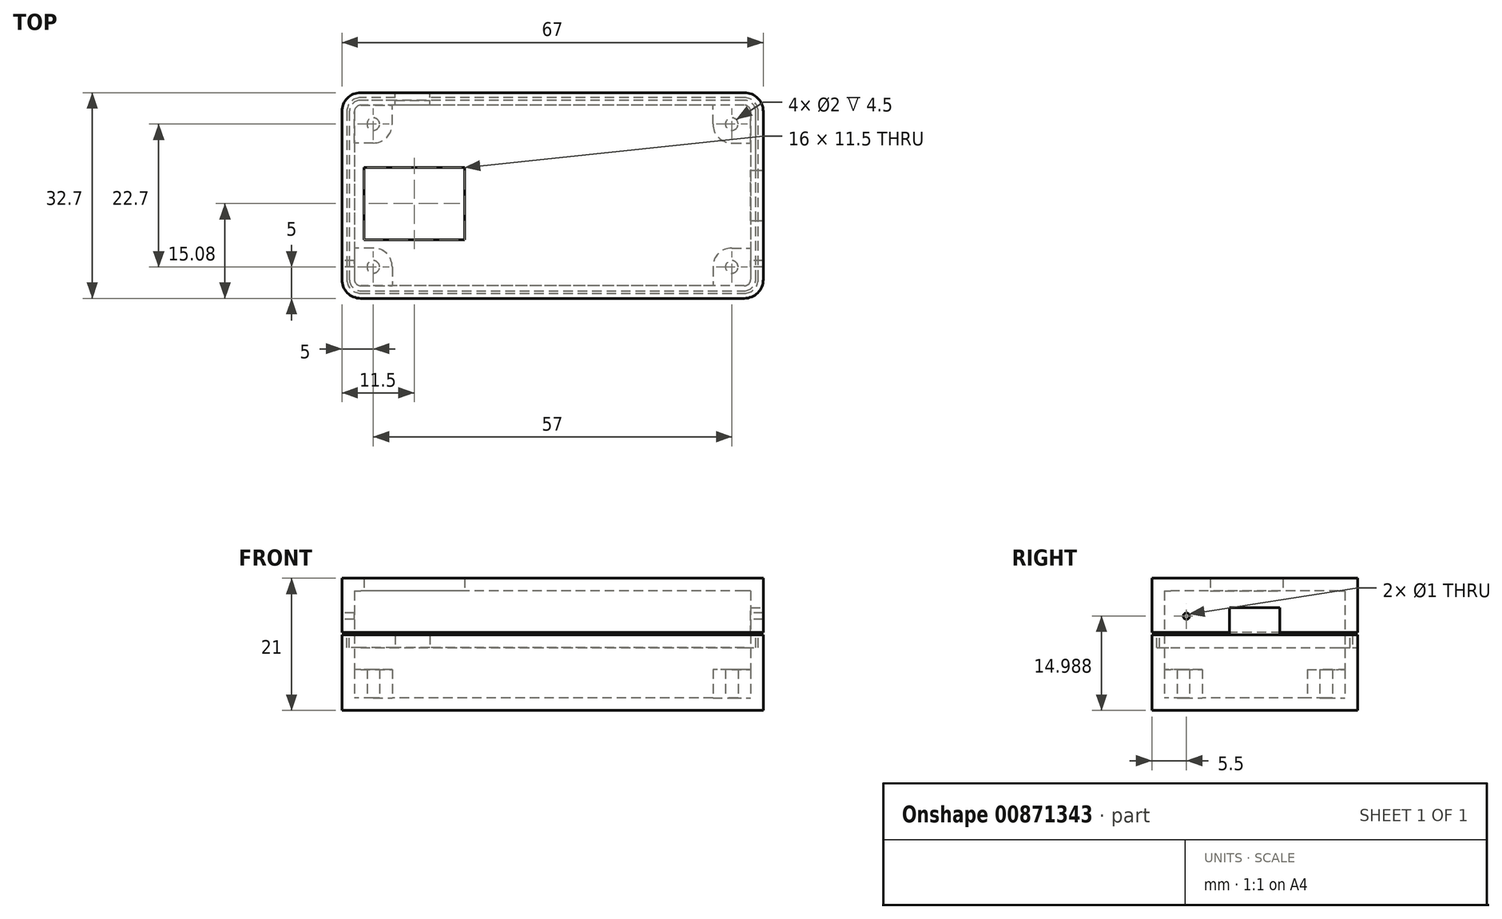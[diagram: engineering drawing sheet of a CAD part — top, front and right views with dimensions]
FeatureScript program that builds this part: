
annotation { "Feature Type Name" : "Feature", "Feature Type Description" : "" }
export const myFeature = defineFeature(function(context is Context, id is Id, definition is map)
    precondition{}
    {
        {
            var Q0;
            Q0=qCreatedBy(makeId("Top.planeOp"),FACE);
            var sketch = newSketch(context, id + "F0", { "sketchPlane" : qUnion([Q0])});
            skLineSegment(sketch, "E0.bottom", {"start": v(33.5, 16.35) * mm, "end": v(-33.5, 16.35) * mm});
            skLineSegment(sketch, "E0.top", {"start": v(33.5, -16.35) * mm, "end": v(-33.5, -16.35) * mm});
            skLineSegment(sketch, "E0.left", {"start": v(33.5, 16.35) * mm, "end": v(33.5, -16.35) * mm});
            skLineSegment(sketch, "E0.right", {"start": v(-33.5, 16.35) * mm, "end": v(-33.5, -16.35) * mm});
            skPoint(sketch, "E0.middle", {"position": v(0, 0) * mm});
            skSolve(sketch);
        }
        {
            var Q0;
            Q0=makeQuery(id+"F0.imprint","IMPRINT",FACE,{"disambiguationData":[TD([[makeQuery(id+"F0.imprint","IMPRINT",EDGE,{"derivedFrom":sQuery(id+"F0.wireOp",EDGE,"E0.bottom")}),1.0]])]});
            extrude(context, id + "F1", {"entities" : qUnion([Q0]), "depth" : 11 * mm, "offsetDistance" : 25 * mm});
        }
        {
            var Q0;
            Q0=makeQuery(id+"F1.opExtrude","SWEPT_EDGE",EDGE,{"disambiguationData":[OSD([sQuery(id+"F0.wireOp",EDGE,"E0.top"),sQuery(id+"F0.wireOp",EDGE,"E0.left")])]});
            var Q1;
            Q1=makeQuery(id+"F1.opExtrude","SWEPT_EDGE",EDGE,{"disambiguationData":[OSD([sQuery(id+"F0.wireOp",EDGE,"E0.bottom"),sQuery(id+"F0.wireOp",EDGE,"E0.left")])]});
            var Q2;
            Q2=makeQuery(id+"F1.opExtrude","SWEPT_EDGE",EDGE,{"disambiguationData":[OSD([sQuery(id+"F0.wireOp",EDGE,"E0.top"),sQuery(id+"F0.wireOp",EDGE,"E0.right")])]});
            var Q3;
            Q3=makeQuery(id+"F1.opExtrude","SWEPT_EDGE",EDGE,{"disambiguationData":[OSD([sQuery(id+"F0.wireOp",EDGE,"E0.bottom"),sQuery(id+"F0.wireOp",EDGE,"E0.right")])]});
            fillet(context, id + "F2", {"entities" : qUnion([Q0, Q1, Q2, Q3]), "radius" : 3 * mm, "tangentPropagation" : true, "allowEdgeOverflow" : false});
        }
        {
            var Q0;
            Q0=makeQuery(id+"F1.opExtrude","CAP_FACE",FACE,{"disambiguationData":[OSD([sQuery(id+"F0.wireOp",EDGE,"E0.bottom"),sQuery(id+"F0.wireOp",EDGE,"E0.top"),sQuery(id+"F0.wireOp",EDGE,"E0.left"),sQuery(id+"F0.wireOp",EDGE,"E0.right")])],"isStart":true});
            extrude(context, id + "F3", {"entities" : qUnion([Q0]), "depth" : 10 * mm, "offsetDistance" : 25 * mm});
        }
        {
            var Q0;
            Q0=makeQuery(id+"F1.opExtrude","CAP_FACE",FACE,{"disambiguationData":[OSD([sQuery(id+"F0.wireOp",EDGE,"E0.bottom"),sQuery(id+"F0.wireOp",EDGE,"E0.top"),sQuery(id+"F0.wireOp",EDGE,"E0.left"),sQuery(id+"F0.wireOp",EDGE,"E0.right")])],"isStart":true});
            shell(context, id + "F4", {"entities" : qUnion([Q0]), "thickness" : 2 * mm});
        }
        {
            var Q0;
            Q0=makeQuery(id+"F3.opExtrude","CAP_FACE",FACE,{"disambiguationData":[OSD([sQuery(id+"F0.wireOp",EDGE,"E0.bottom"),sQuery(id+"F0.wireOp",EDGE,"E0.top"),sQuery(id+"F0.wireOp",EDGE,"E0.left"),sQuery(id+"F0.wireOp",EDGE,"E0.right")])],"isStart":true});
            shell(context, id + "F5", {"entities" : qUnion([Q0]), "thickness" : 2 * mm});
        }
        {
            var Q0;
            Q0=makeQuery(id+"F0.imprint","IMPRINT",FACE,{"disambiguationData":[TD([[makeQuery(id+"F0.imprint","IMPRINT",EDGE,{"derivedFrom":sQuery(id+"F0.wireOp",EDGE,"E0.bottom")}),1.0]])]});
            extrude(context, id + "F6", {"entities" : qUnion([Q0]), "operationType" : NewBodyOperationType.REMOVE, "depth" : 2.4 * mm, "offsetDistance" : 25 * mm});
        }
        {
            var Q0;
            Q0=qCreatedBy(makeId("Right.planeOp"),FACE);
            var sketch = newSketch(context, id + "F7", { "sketchPlane" : qUnion([Q0])});
            skLineSegment(sketch, "E1.bottom", {"start": v(-16.35, 0) * mm, "end": v(-15.55, 0) * mm});
            skLineSegment(sketch, "E1.top", {"start": v(-16.35, 2) * mm, "end": v(-15.55, 2) * mm});
            skLineSegment(sketch, "E1.left", {"start": v(-16.35, 0) * mm, "end": v(-16.35, 2) * mm});
            skLineSegment(sketch, "E1.right", {"start": v(-15.55, 0) * mm, "end": v(-15.55, 2) * mm});
            skLineSegment(sketch, "E2.bottom", {"start": v(-14.35, 0) * mm, "end": v(-15.15, 0) * mm});
            skLineSegment(sketch, "E2.top", {"start": v(-14.35, 2.4) * mm, "end": v(-15.15, 2.4) * mm});
            skLineSegment(sketch, "E2.left", {"start": v(-14.35, 0) * mm, "end": v(-14.35, 2.4) * mm});
            skLineSegment(sketch, "E2.right", {"start": v(-15.15, 0) * mm, "end": v(-15.15, 2.4) * mm});
            skSolve(sketch);
        }
        {
            var Q0;
            Q0=makeQuery(id+"F7.imprint","IMPRINT",FACE,{"disambiguationData":[TD([[makeQuery(id+"F7.imprint","IMPRINT",EDGE,{"derivedFrom":sQuery(id+"F7.wireOp",EDGE,"E1.bottom")}),1.0]])]});
            var Q1;
            Q1=makeQuery(id+"F3.opExtrude","CAP_EDGE",EDGE,{"disambiguationData":[OSD([sQuery(id+"F0.wireOp",EDGE,"E0.top")])],"isStart":true});
            var Q2;
            {var subQ0=sQuery(id+"F0.wireOp",EDGE,"E0.right");var subQ1=sQuery(id+"F0.wireOp",EDGE,"E0.left");var subQ2=sQuery(id+"F0.wireOp",EDGE,"E0.top");var subQ3=sQuery(id+"F0.wireOp",EDGE,"E0.bottom");Q2=makeQuery(id+"F3.opExtrude","CAP_EDGE",EDGE,{"disambiguationData":[OSD([subQ3,subQ2,subQ1,subQ0]),TDD([makeQuery(id+"F2.opFillet","BLEND_EDGE",EDGE,{"blendedFrom":[makeQuery(id+"F1.opExtrude","SWEPT_EDGE",EDGE,{"disambiguationData":[OSD([subQ2,subQ1])]}),makeQuery(id+"F1.opExtrude","CAP_FACE",FACE,{"disambiguationData":[OSD([subQ3,subQ2,subQ1,subQ0])],"isStart":true})],"blendedInto":[makeQuery(id+"F1.opExtrude","CAP_FACE",FACE,{"disambiguationData":[OSD([subQ3,subQ2,subQ1,subQ0])],"isStart":true})]})])],"isStart":true});}
            var Q3;
            Q3=makeQuery(id+"F3.opExtrude","CAP_EDGE",EDGE,{"disambiguationData":[OSD([sQuery(id+"F0.wireOp",EDGE,"E0.left")])],"isStart":true});
            var Q4;
            {var subQ0=sQuery(id+"F0.wireOp",EDGE,"E0.right");var subQ1=sQuery(id+"F0.wireOp",EDGE,"E0.left");var subQ2=sQuery(id+"F0.wireOp",EDGE,"E0.top");var subQ3=sQuery(id+"F0.wireOp",EDGE,"E0.bottom");Q4=makeQuery(id+"F3.opExtrude","CAP_EDGE",EDGE,{"disambiguationData":[OSD([subQ3,subQ2,subQ1,subQ0]),TDD([makeQuery(id+"F2.opFillet","BLEND_EDGE",EDGE,{"blendedFrom":[makeQuery(id+"F1.opExtrude","SWEPT_EDGE",EDGE,{"disambiguationData":[OSD([subQ3,subQ1])]}),makeQuery(id+"F1.opExtrude","CAP_FACE",FACE,{"disambiguationData":[OSD([subQ3,subQ2,subQ1,subQ0])],"isStart":true})],"blendedInto":[makeQuery(id+"F1.opExtrude","CAP_FACE",FACE,{"disambiguationData":[OSD([subQ3,subQ2,subQ1,subQ0])],"isStart":true})]})])],"isStart":true});}
            var Q5;
            Q5=makeQuery(id+"F3.opExtrude","CAP_EDGE",EDGE,{"disambiguationData":[OSD([sQuery(id+"F0.wireOp",EDGE,"E0.bottom")])],"isStart":true});
            var Q6;
            {var subQ0=sQuery(id+"F0.wireOp",EDGE,"E0.right");var subQ1=sQuery(id+"F0.wireOp",EDGE,"E0.left");var subQ2=sQuery(id+"F0.wireOp",EDGE,"E0.top");var subQ3=sQuery(id+"F0.wireOp",EDGE,"E0.bottom");Q6=makeQuery(id+"F3.opExtrude","CAP_EDGE",EDGE,{"disambiguationData":[OSD([subQ3,subQ2,subQ1,subQ0]),TDD([makeQuery(id+"F2.opFillet","BLEND_EDGE",EDGE,{"blendedFrom":[makeQuery(id+"F1.opExtrude","SWEPT_EDGE",EDGE,{"disambiguationData":[OSD([subQ3,subQ0])]}),makeQuery(id+"F1.opExtrude","CAP_FACE",FACE,{"disambiguationData":[OSD([subQ3,subQ2,subQ1,subQ0])],"isStart":true})],"blendedInto":[makeQuery(id+"F1.opExtrude","CAP_FACE",FACE,{"disambiguationData":[OSD([subQ3,subQ2,subQ1,subQ0])],"isStart":true})]})])],"isStart":true});}
            var Q7;
            Q7=makeQuery(id+"F3.opExtrude","CAP_EDGE",EDGE,{"disambiguationData":[OSD([sQuery(id+"F0.wireOp",EDGE,"E0.right")])],"isStart":true});
            var Q8;
            {var subQ0=sQuery(id+"F0.wireOp",EDGE,"E0.right");var subQ1=sQuery(id+"F0.wireOp",EDGE,"E0.left");var subQ2=sQuery(id+"F0.wireOp",EDGE,"E0.top");var subQ3=sQuery(id+"F0.wireOp",EDGE,"E0.bottom");Q8=makeQuery(id+"F3.opExtrude","CAP_EDGE",EDGE,{"disambiguationData":[OSD([subQ3,subQ2,subQ1,subQ0]),TDD([makeQuery(id+"F2.opFillet","BLEND_EDGE",EDGE,{"blendedFrom":[makeQuery(id+"F1.opExtrude","SWEPT_EDGE",EDGE,{"disambiguationData":[OSD([subQ2,subQ0])]}),makeQuery(id+"F1.opExtrude","CAP_FACE",FACE,{"disambiguationData":[OSD([subQ3,subQ2,subQ1,subQ0])],"isStart":true})],"blendedInto":[makeQuery(id+"F1.opExtrude","CAP_FACE",FACE,{"disambiguationData":[OSD([subQ3,subQ2,subQ1,subQ0])],"isStart":true})]})])],"isStart":true});}
            sweep(context, id + "F8", {"operationType" : NewBodyOperationType.ADD, "profiles" : qUnion([Q0]), "path" : qUnion([Q1, Q2, Q3, Q4, Q5, Q6, Q7, Q8])});
        }
        {
            var Q0;
            Q0=makeQuery(id+"F7.imprint","IMPRINT",FACE,{"disambiguationData":[TD([[makeQuery(id+"F7.imprint","IMPRINT",EDGE,{"derivedFrom":sQuery(id+"F7.wireOp",EDGE,"E2.bottom")}),-1.0]])]});
            var Q1;
            Q1=makeQuery(id+"F8.opSweep","SWEPT_EDGE",EDGE,{"disambiguationData":[OSD([sQuery(id+"F0.wireOp",EDGE,"E0.top"),sQuery(id+"F7.wireOp",EDGE,"E1.top"),sQuery(id+"F7.wireOp",EDGE,"E1.left")])]});
            var Q2;
            {var subQ0=sQuery(id+"F7.wireOp",EDGE,"E1.left");var subQ1=sQuery(id+"F7.wireOp",EDGE,"E1.top");var subQ2=sQuery(id+"F0.wireOp",EDGE,"E0.right");var subQ3=sQuery(id+"F0.wireOp",EDGE,"E0.left");var subQ4=sQuery(id+"F0.wireOp",EDGE,"E0.top");var subQ5=sQuery(id+"F0.wireOp",EDGE,"E0.bottom");Q2=makeQuery(id+"F8.opSweep","SWEPT_EDGE",EDGE,{"disambiguationData":[OSD([subQ5,subQ4,subQ3,subQ2,subQ1,subQ0]),TDD([makeQuery(id+"F3.opExtrude","CAP_EDGE",EDGE,{"disambiguationData":[OSD([subQ5,subQ4,subQ3,subQ2]),TDD([makeQuery(id+"F2.opFillet","BLEND_EDGE",EDGE,{"blendedFrom":[makeQuery(id+"F1.opExtrude","SWEPT_EDGE",EDGE,{"disambiguationData":[OSD([subQ4,subQ3])]}),makeQuery(id+"F1.opExtrude","CAP_FACE",FACE,{"disambiguationData":[OSD([subQ5,subQ4,subQ3,subQ2])],"isStart":true})],"blendedInto":[makeQuery(id+"F1.opExtrude","CAP_FACE",FACE,{"disambiguationData":[OSD([subQ5,subQ4,subQ3,subQ2])],"isStart":true})]})])],"isStart":true}),makeQuery(id+"F7.imprint","INTERSECT",VERTEX,{"derivedFrom":[subQ1,subQ0]})])]});}
            var Q3;
            Q3=makeQuery(id+"F8.opSweep","SWEPT_EDGE",EDGE,{"disambiguationData":[OSD([sQuery(id+"F0.wireOp",EDGE,"E0.left"),sQuery(id+"F7.wireOp",EDGE,"E1.top"),sQuery(id+"F7.wireOp",EDGE,"E1.left")])]});
            var Q4;
            {var subQ0=sQuery(id+"F7.wireOp",EDGE,"E1.left");var subQ1=sQuery(id+"F7.wireOp",EDGE,"E1.top");var subQ2=sQuery(id+"F0.wireOp",EDGE,"E0.right");var subQ3=sQuery(id+"F0.wireOp",EDGE,"E0.left");var subQ4=sQuery(id+"F0.wireOp",EDGE,"E0.top");var subQ5=sQuery(id+"F0.wireOp",EDGE,"E0.bottom");Q4=makeQuery(id+"F8.opSweep","SWEPT_EDGE",EDGE,{"disambiguationData":[OSD([subQ5,subQ4,subQ3,subQ2,subQ1,subQ0]),TDD([makeQuery(id+"F3.opExtrude","CAP_EDGE",EDGE,{"disambiguationData":[OSD([subQ5,subQ4,subQ3,subQ2]),TDD([makeQuery(id+"F2.opFillet","BLEND_EDGE",EDGE,{"blendedFrom":[makeQuery(id+"F1.opExtrude","SWEPT_EDGE",EDGE,{"disambiguationData":[OSD([subQ5,subQ3])]}),makeQuery(id+"F1.opExtrude","CAP_FACE",FACE,{"disambiguationData":[OSD([subQ5,subQ4,subQ3,subQ2])],"isStart":true})],"blendedInto":[makeQuery(id+"F1.opExtrude","CAP_FACE",FACE,{"disambiguationData":[OSD([subQ5,subQ4,subQ3,subQ2])],"isStart":true})]})])],"isStart":true}),makeQuery(id+"F7.imprint","INTERSECT",VERTEX,{"derivedFrom":[subQ1,subQ0]})])]});}
            var Q5;
            Q5=makeQuery(id+"F8.opSweep","SWEPT_EDGE",EDGE,{"disambiguationData":[OSD([sQuery(id+"F0.wireOp",EDGE,"E0.bottom"),sQuery(id+"F7.wireOp",EDGE,"E1.top"),sQuery(id+"F7.wireOp",EDGE,"E1.left")])]});
            var Q6;
            {var subQ0=sQuery(id+"F7.wireOp",EDGE,"E1.left");var subQ1=sQuery(id+"F7.wireOp",EDGE,"E1.top");var subQ2=sQuery(id+"F0.wireOp",EDGE,"E0.right");var subQ3=sQuery(id+"F0.wireOp",EDGE,"E0.left");var subQ4=sQuery(id+"F0.wireOp",EDGE,"E0.top");var subQ5=sQuery(id+"F0.wireOp",EDGE,"E0.bottom");Q6=makeQuery(id+"F8.opSweep","SWEPT_EDGE",EDGE,{"disambiguationData":[OSD([subQ5,subQ4,subQ3,subQ2,subQ1,subQ0]),TDD([makeQuery(id+"F3.opExtrude","CAP_EDGE",EDGE,{"disambiguationData":[OSD([subQ5,subQ4,subQ3,subQ2]),TDD([makeQuery(id+"F2.opFillet","BLEND_EDGE",EDGE,{"blendedFrom":[makeQuery(id+"F1.opExtrude","SWEPT_EDGE",EDGE,{"disambiguationData":[OSD([subQ5,subQ2])]}),makeQuery(id+"F1.opExtrude","CAP_FACE",FACE,{"disambiguationData":[OSD([subQ5,subQ4,subQ3,subQ2])],"isStart":true})],"blendedInto":[makeQuery(id+"F1.opExtrude","CAP_FACE",FACE,{"disambiguationData":[OSD([subQ5,subQ4,subQ3,subQ2])],"isStart":true})]})])],"isStart":true}),makeQuery(id+"F7.imprint","INTERSECT",VERTEX,{"derivedFrom":[subQ1,subQ0]})])]});}
            var Q7;
            Q7=makeQuery(id+"F8.opSweep","SWEPT_EDGE",EDGE,{"disambiguationData":[OSD([sQuery(id+"F0.wireOp",EDGE,"E0.right"),sQuery(id+"F7.wireOp",EDGE,"E1.top"),sQuery(id+"F7.wireOp",EDGE,"E1.left")])]});
            var Q8;
            {var subQ0=sQuery(id+"F7.wireOp",EDGE,"E1.left");var subQ1=sQuery(id+"F7.wireOp",EDGE,"E1.top");var subQ2=sQuery(id+"F0.wireOp",EDGE,"E0.right");var subQ3=sQuery(id+"F0.wireOp",EDGE,"E0.left");var subQ4=sQuery(id+"F0.wireOp",EDGE,"E0.top");var subQ5=sQuery(id+"F0.wireOp",EDGE,"E0.bottom");Q8=makeQuery(id+"F8.opSweep","SWEPT_EDGE",EDGE,{"disambiguationData":[OSD([subQ5,subQ4,subQ3,subQ2,subQ1,subQ0]),TDD([makeQuery(id+"F3.opExtrude","CAP_EDGE",EDGE,{"disambiguationData":[OSD([subQ5,subQ4,subQ3,subQ2]),TDD([makeQuery(id+"F2.opFillet","BLEND_EDGE",EDGE,{"blendedFrom":[makeQuery(id+"F1.opExtrude","SWEPT_EDGE",EDGE,{"disambiguationData":[OSD([subQ4,subQ2])]}),makeQuery(id+"F1.opExtrude","CAP_FACE",FACE,{"disambiguationData":[OSD([subQ5,subQ4,subQ3,subQ2])],"isStart":true})],"blendedInto":[makeQuery(id+"F1.opExtrude","CAP_FACE",FACE,{"disambiguationData":[OSD([subQ5,subQ4,subQ3,subQ2])],"isStart":true})]})])],"isStart":true}),makeQuery(id+"F7.imprint","INTERSECT",VERTEX,{"derivedFrom":[subQ1,subQ0]})])]});}
            sweep(context, id + "F9", {"operationType" : NewBodyOperationType.ADD, "profiles" : qUnion([Q0]), "path" : qUnion([Q1, Q2, Q3, Q4, Q5, Q6, Q7, Q8])});
        }
        {
            var Q0;
            {var subQ0=sQuery(id+"F0.wireOp",EDGE,"E0.right");var subQ1=sQuery(id+"F0.wireOp",EDGE,"E0.left");var subQ2=sQuery(id+"F0.wireOp",EDGE,"E0.top");var subQ3=sQuery(id+"F0.wireOp",EDGE,"E0.bottom");Q0=makeQuery(id+"F5.opShell","OFFSET_FACE",FACE,{"disambiguationData":[OSD([subQ3,subQ2,subQ1,subQ0]),TDD([makeQuery(id+"F3.opExtrude","CAP_FACE",FACE,{"disambiguationData":[OSD([subQ3,subQ2,subQ1,subQ0])],"isStart":false})])]});}
            var sketch = newSketch(context, id + "F10", { "sketchPlane" : qUnion([Q0])});
            skCircle(sketch, "E3", {"center": v(-28.5, -11.35) * mm, "radius": 3 * mm});
            skCircle(sketch, "E4", {"center": v(-28.5, -11.35) * mm, "radius": 1 * mm});
            skLineSegment(sketch, "E5", {"start": v(-25.5, -11.35) * mm, "end": v(-25.5, -14.35) * mm});
            skLineSegment(sketch, "E6", {"start": v(-28.5, -8.35) * mm, "end": v(-31.5, -8.35) * mm});
            skLineSegment(sketch, "E7", {"start": v(-31.5, -8.35) * mm, "end": v(-31.5, -14.35) * mm});
            skLineSegment(sketch, "E8", {"start": v(-31.5, -14.35) * mm, "end": v(-25.5, -14.35) * mm});
            skLineSegment(sketch, "E9.MirrorCS", {"start": v(-25.5, 11.35) * mm, "end": v(-25.5, 14.35) * mm});
            skLineSegment(sketch, "E10.MirrorCS", {"start": v(-31.5, 14.35) * mm, "end": v(-25.5, 14.35) * mm});
            skCircle(sketch, "E11.MirrorC", {"center": v(-28.5, 11.35) * mm, "radius": 3 * mm});
            skLineSegment(sketch, "E12.MirrorCS", {"start": v(-28.5, 8.35) * mm, "end": v(-31.5, 8.35) * mm});
            skLineSegment(sketch, "E13.MirrorCS", {"start": v(-31.5, 8.35) * mm, "end": v(-31.5, 14.35) * mm});
            skCircle(sketch, "E14.MirrorC", {"center": v(28.5, -11.35) * mm, "radius": 3 * mm});
            skLineSegment(sketch, "E15.MirrorCS", {"start": v(25.5, -11.35) * mm, "end": v(25.5, -14.35) * mm});
            skLineSegment(sketch, "E16.MirrorCS", {"start": v(31.5, -14.35) * mm, "end": v(25.5, -14.35) * mm});
            skLineSegment(sketch, "E17.MirrorCS", {"start": v(31.5, -8.35) * mm, "end": v(31.5, -14.35) * mm});
            skLineSegment(sketch, "E18.MirrorCS", {"start": v(28.5, -8.35) * mm, "end": v(31.5, -8.35) * mm});
            skLineSegment(sketch, "E19.MirrorCS", {"start": v(28.5, 8.35) * mm, "end": v(31.5, 8.35) * mm});
            skLineSegment(sketch, "E20.MirrorCS", {"start": v(25.5, 11.35) * mm, "end": v(25.5, 14.35) * mm});
            skLineSegment(sketch, "E21.MirrorCS", {"start": v(31.5, 8.35) * mm, "end": v(31.5, 14.35) * mm});
            skLineSegment(sketch, "E22.MirrorCS", {"start": v(31.5, 14.35) * mm, "end": v(25.5, 14.35) * mm});
            skCircle(sketch, "E23.MirrorC", {"center": v(28.5, 11.35) * mm, "radius": 3 * mm});
            skCircle(sketch, "E24.MirrorC", {"center": v(-28.5, 11.35) * mm, "radius": 1 * mm});
            skCircle(sketch, "E25.MirrorC", {"center": v(28.5, -11.35) * mm, "radius": 1 * mm});
            skCircle(sketch, "E26.MirrorC", {"center": v(28.5, 11.35) * mm, "radius": 1 * mm});
            skSolve(sketch);
        }
        {
            var Q0;
            Q0 = qSketchRegion(id + "F10", true);
            extrude(context, id + "F11", {"entities" : qUnion([Q0]), "operationType" : NewBodyOperationType.ADD, "depth" : 4.5 * mm, "offsetDistance" : 25 * mm});
        }
        {
            var Q0;
            Q0=qCreatedBy(makeId("Top.planeOp"),FACE);
            var sketch = newSketch(context, id + "F12", { "sketchPlane" : qUnion([Q0])});
            skLineSegment(sketch, "E27.bottom", {"start": v(-30, 4.48) * mm, "end": v(-14, 4.48) * mm});
            skLineSegment(sketch, "E27.top", {"start": v(-30, -7.02) * mm, "end": v(-14, -7.02) * mm});
            skLineSegment(sketch, "E27.left", {"start": v(-30, 4.48) * mm, "end": v(-30, -7.02) * mm});
            skLineSegment(sketch, "E27.right", {"start": v(-14, 4.48) * mm, "end": v(-14, -7.02) * mm});
            skLineSegment(sketch, "E28", {"start": v(-30, -1.27) * mm, "end": v(-14, -1.27) * mm, "construction": true});
            skSolve(sketch);
        }
        {
            var Q0;
            Q0=makeQuery(id+"F12.imprint","IMPRINT",FACE,{"disambiguationData":[TD([[makeQuery(id+"F12.imprint","IMPRINT",EDGE,{"derivedFrom":sQuery(id+"F12.wireOp",EDGE,"E27.bottom")}),-1.0]])]});
            extrude(context, id + "F13", {"entities" : qUnion([Q0]), "operationType" : NewBodyOperationType.REMOVE, "endBound" : BoundingType.THROUGH_ALL, "depth" : 25 * mm, "offsetDistance" : 25 * mm});
        }
        {
            var Q0;
            Q0=makeQuery(id+"F1.opExtrude","SWEPT_FACE",FACE,{"disambiguationData":[OSD([sQuery(id+"F0.wireOp",EDGE,"E0.right")])]});
            var sketch = newSketch(context, id + "F14", { "sketchPlane" : qUnion([Q0])});
            skCircle(sketch, "E29", {"center": v(10.85, 4.99) * mm, "radius": 0.5 * mm});
            skSolve(sketch);
        }
        {
            var Q0;
            Q0=makeQuery(id+"F14.imprint","IMPRINT",FACE,{"disambiguationData":[TD([[makeQuery(id+"F14.imprint","IMPRINT",EDGE,{"derivedFrom":sQuery(id+"F14.wireOp",EDGE,"E29")}),1.0]])]});
            extrude(context, id + "F15", {"entities" : qUnion([Q0]), "operationType" : NewBodyOperationType.REMOVE, "endBound" : BoundingType.THROUGH_ALL, "oppositeDirection" : true, "depth" : 25 * mm, "offsetDistance" : 25 * mm});
        }
        {
            var Q0;
            {var subQ0=sQuery(id+"F0.wireOp",EDGE,"E0.left");Q0=makeQuery(id+"F8.boolean.opBoolean","MERGE",FACE,{"derivedFrom":[makeQuery(id+"F3.opExtrude","SWEPT_FACE",FACE,{"disambiguationData":[OSD([subQ0])]}),makeQuery(id+"F8.opSweep","SWEPT_FACE",FACE,{"disambiguationData":[OSD([subQ0,sQuery(id+"F7.wireOp",EDGE,"E1.left")])]})]});}
            var sketch = newSketch(context, id + "F16", { "sketchPlane" : qUnion([Q0])});
            skLineSegment(sketch, "E30.bottom", {"start": v(4, 6.3) * mm, "end": v(-4, 6.3) * mm});
            skLineSegment(sketch, "E30.top", {"start": v(4, 1.8) * mm, "end": v(-4, 1.8) * mm});
            skLineSegment(sketch, "E30.left", {"start": v(4, 6.3) * mm, "end": v(4, 1.8) * mm});
            skLineSegment(sketch, "E30.right", {"start": v(-4, 6.3) * mm, "end": v(-4, 1.8) * mm});
            skPoint(sketch, "E30.middle", {"position": v(0, 4.05) * mm});
            skSolve(sketch);
        }
        {
            var Q0;
            Q0=makeQuery(id+"F16.imprint","IMPRINT",FACE,{"disambiguationData":[TD([[makeQuery(id+"F16.imprint","IMPRINT",EDGE,{"derivedFrom":sQuery(id+"F16.wireOp",EDGE,"E30.bottom")}),1.0]])]});
            extrude(context, id + "F17", {"entities" : qUnion([Q0]), "operationType" : NewBodyOperationType.REMOVE, "endBound" : BoundingType.UP_TO_NEXT, "oppositeDirection" : true, "depth" : 25 * mm, "offsetDistance" : 25 * mm});
        }
        {
            var Q0;
            Q0=makeQuery(id+"F1.opExtrude","SWEPT_FACE",FACE,{"disambiguationData":[OSD([sQuery(id+"F0.wireOp",EDGE,"E0.bottom")])]});
            var sketch = newSketch(context, id + "F18", { "sketchPlane" : qUnion([Q0])});
            skLineSegment(sketch, "E31.bottom", {"start": v(25, 0) * mm, "end": v(19.5, 0) * mm});
            skLineSegment(sketch, "E31.top", {"start": v(25, 2) * mm, "end": v(19.5, 2) * mm});
            skLineSegment(sketch, "E31.left", {"start": v(25, 0) * mm, "end": v(25, 2) * mm});
            skLineSegment(sketch, "E31.right", {"start": v(19.5, 0) * mm, "end": v(19.5, 2) * mm});
            skPoint(sketch, "E31.middle", {"position": v(22.25, 1) * mm});
            skSolve(sketch);
        }
        {
            var Q0;
            Q0=makeQuery(id+"F18.imprint","IMPRINT",FACE,{"disambiguationData":[TD([[makeQuery(id+"F18.imprint","IMPRINT",EDGE,{"derivedFrom":sQuery(id+"F18.wireOp",EDGE,"E31.bottom")}),-1.0]])]});
            extrude(context, id + "F19", {"entities" : qUnion([Q0]), "operationType" : NewBodyOperationType.REMOVE, "oppositeDirection" : true, "depth" : 2.4 * mm, "offsetDistance" : 25 * mm});
        }
    });
